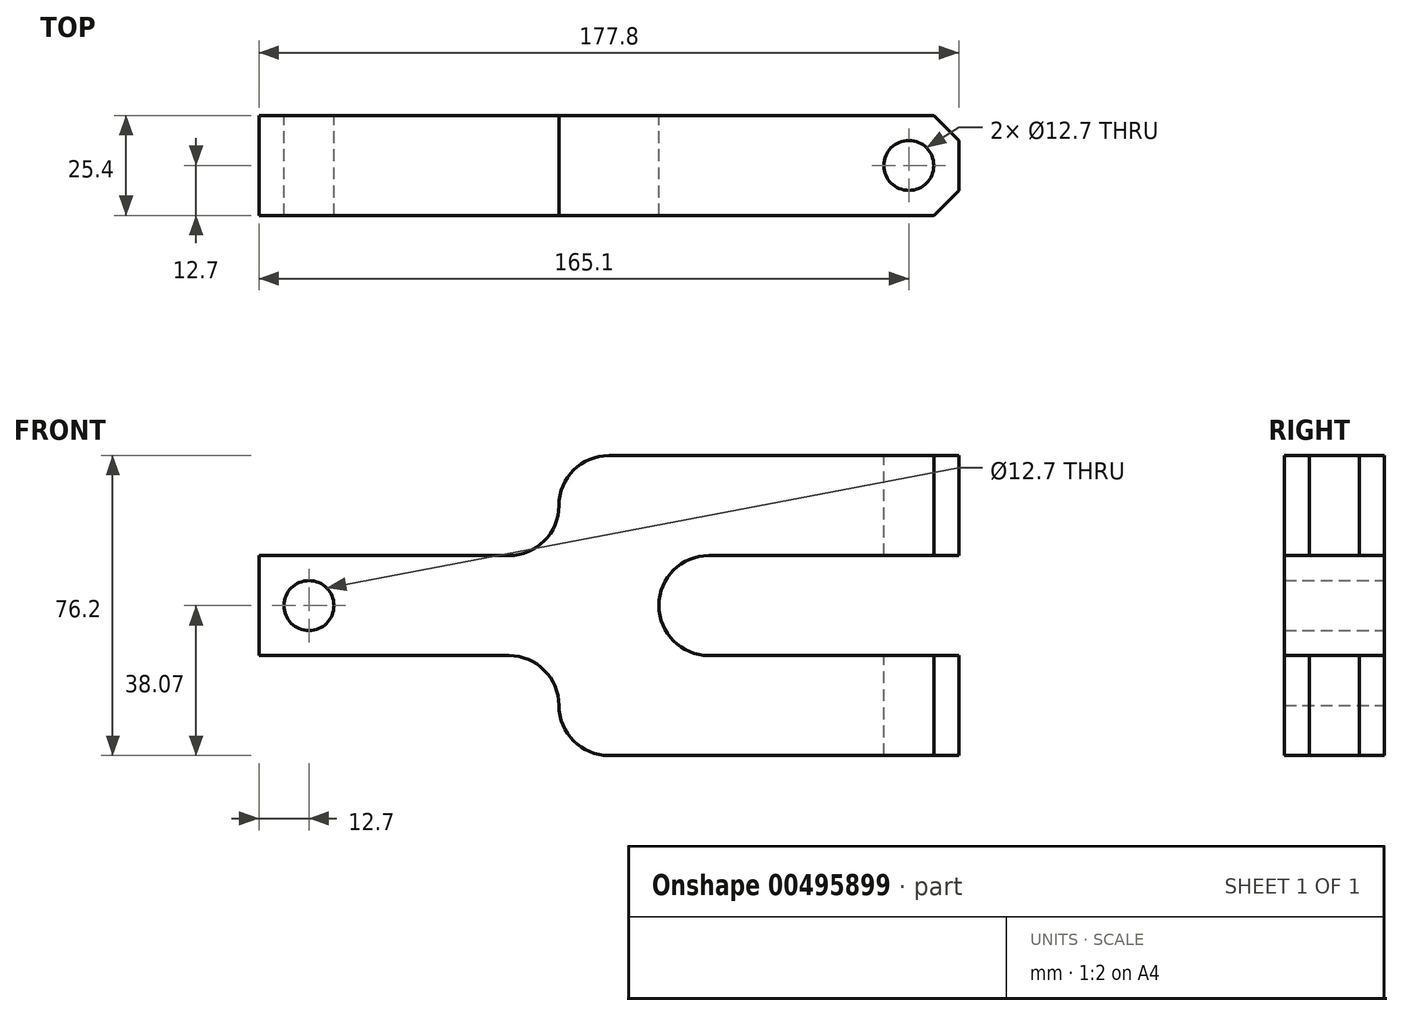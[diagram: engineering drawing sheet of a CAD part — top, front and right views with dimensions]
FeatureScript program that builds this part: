
annotation { "Feature Type Name" : "Feature", "Feature Type Description" : "" }
export const myFeature = defineFeature(function(context is Context, id is Id, definition is map)
    precondition{}
    {
        {
            var Q0;
            Q0=qCreatedBy(makeId("Front.planeOp"),FACE);
            var sketch = newSketch(context, id + "F0", { "sketchPlane" : qUnion([Q0])});
            skLineSegment(sketch, "E0.bottom", {"start": v(-76.2, 12.7) * mm, "end": v(-12.7, 12.7) * mm});
            skLineSegment(sketch, "E0.top", {"start": v(-76.2, -12.7) * mm, "end": v(-12.7, -12.7) * mm});
            skLineSegment(sketch, "E0.left", {"start": v(-76.2, 12.7) * mm, "end": v(-76.2, -12.7) * mm});
            skLineSegment(sketch, "E0.right", {"start": v(25.4, 0.03) * mm, "end": v(25.4, 0.03) * mm});
            skLineSegment(sketch, "E1.bottom", {"start": v(12.7, 38.13) * mm, "end": v(101.6, 38.13) * mm});
            skLineSegment(sketch, "E1.top", {"start": v(38.1, 12.73) * mm, "end": v(101.6, 12.73) * mm});
            skLineSegment(sketch, "E1.left", {"start": v(0, 25.43) * mm, "end": v(0, 25.4) * mm});
            skLineSegment(sketch, "E1.right", {"start": v(101.6, 38.13) * mm, "end": v(101.6, 12.73) * mm});
            skLineSegment(sketch, "E2.bottom", {"start": v(38.1, -12.67) * mm, "end": v(101.6, -12.67) * mm});
            skLineSegment(sketch, "E2.top", {"start": v(12.7, -38.07) * mm, "end": v(101.6, -38.07) * mm});
            skLineSegment(sketch, "E2.left", {"start": v(0, -25.37) * mm, "end": v(0, -25.4) * mm});
            skLineSegment(sketch, "E2.right", {"start": v(101.6, -12.67) * mm, "end": v(101.6, -38.07) * mm});
            skPoint(sketch, "E3.visualSharp", {"position": v(0, -38.07) * mm});
            skArc(sketch, "E3.filletArc", {"start": v(0, -25.37) * mm, "mid": v(3.72, -34.35) * mm, "end": v(12.7, -38.07) * mm});
            skPoint(sketch, "E4.visualSharp", {"position": v(0, 38.13) * mm});
            skArc(sketch, "E4.filletArc", {"start": v(12.7, 38.13) * mm, "mid": v(3.72, 34.41) * mm, "end": v(0, 25.43) * mm});
            skPoint(sketch, "E5.newPointA", {"position": v(0, -12.7) * mm});
            skArc(sketch, "E5.filletArc", {"start": v(0, -25.4) * mm, "mid": v(-3.72, -16.42) * mm, "end": v(-12.7, -12.7) * mm});
            skPoint(sketch, "E6.newPointA", {"position": v(0, 12.7) * mm});
            skArc(sketch, "E6.filletArc", {"start": v(-12.7, 12.7) * mm, "mid": v(-3.72, 16.42) * mm, "end": v(0, 25.4) * mm});
            skArc(sketch, "E7.filletArc", {"start": v(38.1, 12.73) * mm, "mid": v(29.12, 9.01) * mm, "end": v(25.4, 0.03) * mm});
            skArc(sketch, "E8.filletArc", {"start": v(25.4, 0.03) * mm, "mid": v(29.12, -8.95) * mm, "end": v(38.1, -12.67) * mm});
            skCircle(sketch, "E9", {"center": v(-63.5, 0) * mm, "radius": 6.35 * mm});
            skPoint(sketch, "E10", {"position": v(88.9, 38.13) * mm});
            skSolve(sketch);
        }
        {
            var Q0;
            Q0=qCreatedBy(makeId("Top.planeOp"),FACE);
            var sketch = newSketch(context, id + "F1", { "sketchPlane" : qUnion([Q0])});
            skCircle(sketch, "E11", {"center": v(88.9, 0) * mm, "radius": 6.35 * mm});
            skSolve(sketch);
        }
        {
            var Q0;
            Q0 = qSketchRegion(id + "F0", true);
            extrude(context, id + "F2", {"entities" : qUnion([Q0]), "endBound" : BoundingType.SYMMETRIC, "depth" : 25.4 * mm});
        }
        {
            var Q0;
            Q0=makeQuery(id+"F1.imprint","IMPRINT",FACE,{"disambiguationData":[TD([[makeQuery(id+"F1.imprint","IMPRINT",EDGE,{"derivedFrom":sQuery(id+"F1.wireOp",EDGE,"E11")}),1.0]])]});
            extrude(context, id + "F3", {"entities" : qUnion([Q0]), "operationType" : NewBodyOperationType.REMOVE, "endBound" : BoundingType.SYMMETRIC, "oppositeDirection" : true, "depth" : 88.9 * mm});
        }
        {
            var Q0;
            Q0=makeQuery(id+"F2.opExtrude","CAP_EDGE",EDGE,{"disambiguationData":[OSD([sQuery(id+"F0.wireOp",EDGE,"E1.right")])],"isStart":true});
            chamfer(context, id + "F4", {"entities" : qUnion([Q0]), "width" : 6.35 * mm, "tangentPropagation" : true});
        }
        {
            var Q0;
            Q0=makeQuery(id+"F2.opExtrude","CAP_EDGE",EDGE,{"disambiguationData":[OSD([sQuery(id+"F0.wireOp",EDGE,"E1.right")])],"isStart":false});
            chamfer(context, id + "F5", {"entities" : qUnion([Q0]), "width" : 6.35 * mm, "tangentPropagation" : true});
        }
        {
            var Q0;
            Q0=makeQuery(id+"F2.opExtrude","CAP_EDGE",EDGE,{"disambiguationData":[OSD([sQuery(id+"F0.wireOp",EDGE,"E2.right")])],"isStart":true});
            chamfer(context, id + "F6", {"entities" : qUnion([Q0]), "width" : 6.35 * mm, "tangentPropagation" : true});
        }
        {
            var Q0;
            Q0=makeQuery(id+"F2.opExtrude","CAP_EDGE",EDGE,{"disambiguationData":[OSD([sQuery(id+"F0.wireOp",EDGE,"E2.right")])],"isStart":false});
            chamfer(context, id + "F7", {"entities" : qUnion([Q0]), "width" : 6.35 * mm, "tangentPropagation" : true});
        }
    });
